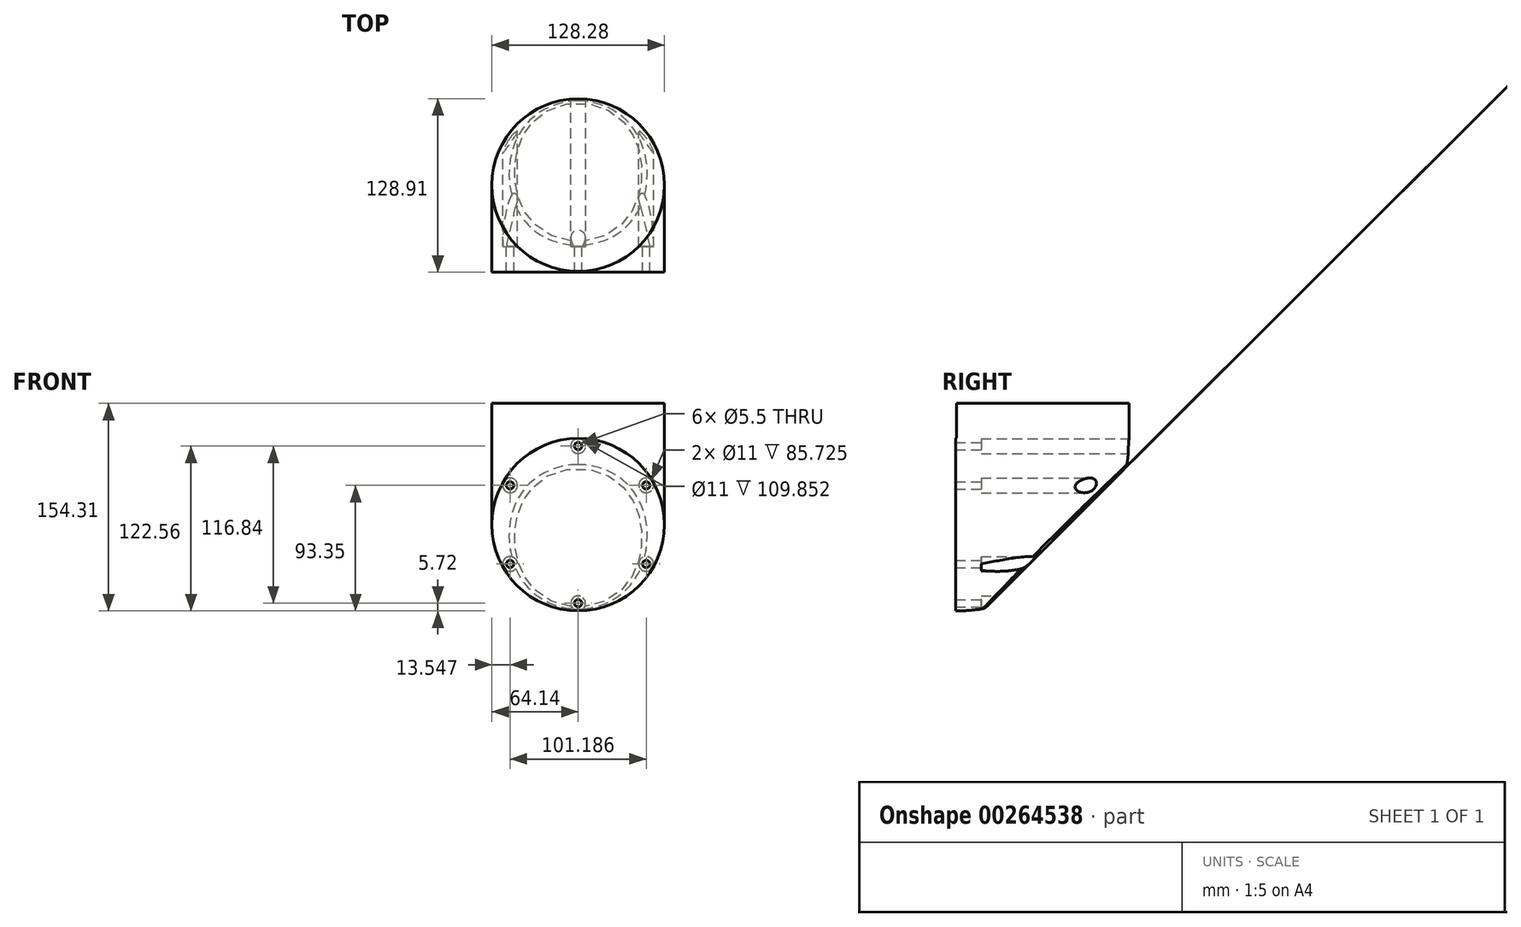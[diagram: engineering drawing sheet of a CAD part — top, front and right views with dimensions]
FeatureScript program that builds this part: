
annotation { "Feature Type Name" : "Feature", "Feature Type Description" : "" }
export const myFeature = defineFeature(function(context is Context, id is Id, definition is map)
    precondition{}
    {
        {
            var Q0;
            Q0=qCreatedBy(makeId("Front.planeOp"),FACE);
            var sketch = newSketch(context, id + "F0", { "sketchPlane" : qUnion([Q0])});
            skCircle(sketch, "E0", {"center": v(0, 0) * mm, "radius": 64.13 * mm});
            skSolve(sketch);
        }
        {
            var Q0;
            Q0=qCreatedBy(makeId("Right.planeOp"),FACE);
            var sketch = newSketch(context, id + "F1", { "sketchPlane" : qUnion([Q0])});
            skArc(sketch, "E1", {"start": v(0, 0) * mm, "mid": v(45.8, 18.97) * mm, "end": v(64.77, 64.77) * mm});
            skLineSegment(sketch, "E2", {"start": v(64.77, 64.77) * mm, "end": v(0, 64.77) * mm, "construction": true});
            skSolve(sketch);
        }
        {
            var Q0;
            Q0 = qSketchRegion(id + "F0", true);
            var Q1;
            Q1 = qConstructionFilter(qBodyType(qCreatedBy(id + "F1" ,EDGE), BodyType.WIRE), ConstructionObject.NO);
            sweep(context, id + "F2", {"profiles" : qUnion([Q0]), "path" : qUnion([Q1])});
        }
        {
            var Q0;
            Q0=qCreatedBy(makeId("Top.planeOp"),FACE);
            cPlane(context, id + "F3", {"entities" : qUnion([Q0]), "cplaneType" : CPlaneType.OFFSET, "offset" : 64.77 * mm, "width" : 152.4 * mm, "height" : 152.4 * mm});
        }
        {
            var Q0;
            Q0=qCreatedBy(id+"F3.planeOp",FACE);
            var sketch = newSketch(context, id + "F4", { "sketchPlane" : qUnion([Q0])});
            skPoint(sketch, "E3", {"position": v(0, 64.77) * mm});
            skLineSegment(sketch, "E4", {"start": v(0, 64.77) * mm, "end": v(0, 0) * mm, "construction": true});
            skCircle(sketch, "E5", {"center": v(0, 64.77) * mm, "radius": 50.8 * mm});
            skSolve(sketch);
        }
        {
            var Q0;
            Q0=makeQuery(id+"F2.opSweep","CAP_FACE",FACE,{"disambiguationData":[OSD([sQuery(id+"F0.wireOp",EDGE,"E0"),sQuery(id+"F1.wireOp",VERTEX,"E1.start")])],"isStart":true});
            var sketch = newSketch(context, id + "F5", { "sketchPlane" : qUnion([Q0])});
            skCircle(sketch, "E6", {"center": v(0, 0) * mm, "radius": 58.42 * mm, "construction": true});
            skPoint(sketch, "E7", {"position": v(0, 58.42) * mm});
            skPoint(sketch, "E8.1.0", {"position": v(-50.6, 29.21) * mm});
            skPoint(sketch, "E8.2.0", {"position": v(-50.6, -29.2) * mm});
            skPoint(sketch, "E8.3.0", {"position": v(0, -58.42) * mm});
            skPoint(sketch, "E8.4.0", {"position": v(50.6, -29.21) * mm});
            skPoint(sketch, "E8.5.0", {"position": v(50.6, 29.21) * mm});
            skSolve(sketch);
        }
        {
            var Q0;
            Q0=sQuery(id+"F5.wireOp",VERTEX,"E7");
            var Q1;
            Q1=sQuery(id+"F5.wireOp",VERTEX,"E8.1.0");
            var Q2;
            Q2=sQuery(id+"F5.wireOp",VERTEX,"E8.2.0");
            var Q3;
            Q3=sQuery(id+"F5.wireOp",VERTEX,"E8.3.0");
            var Q4;
            Q4=sQuery(id+"F5.wireOp",VERTEX,"E8.4.0");
            var Q5;
            Q5=sQuery(id+"F5.wireOp",VERTEX,"E8.5.0");
            var Q6;
            Q6=makeQuery(id+"F2.opSweep","SWEPT_BODY",BODY,{"disambiguationData":[OSD([sQuery(id+"F0.wireOp",EDGE,"E0"),sQuery(id+"F1.wireOp",EDGE,"E1")])]});
            hole(context, id + "F6", {"style" : HoleStyle.SIMPLE, "endStyle" : HoleEndStyle.THROUGH, "standardTappedOrClearance" : lookupTablePath({ "standard" : "ISO", "fit" : "Normal", "size" : "M5", "type" : "Clearance" }), "standardBlindInLast" : lookupTablePath({ "fit" : "Standard", "standard" : "ISO", "size" : "M5", "type" : "Clearance" }), "holeDiameter" : 5.5 * mm, "isTappedThrough" : true, "tappedDepth" : 12.7 * mm, "tapClearance" : 3, "locations" : qUnion([Q0, Q1, Q2, Q3, Q4, Q5]), "scope" : qUnion([Q6]), "startStyle" : HoleStartStyle.PART});
        }
        {
            var Q0;
            Q0=qCreatedBy(makeId("Front.planeOp"),FACE);
            cPlane(context, id + "F7", {"entities" : qUnion([Q0]), "cplaneType" : CPlaneType.OFFSET, "offset" : 19.05 * mm, "oppositeDirection" : true, "width" : 152.4 * mm, "height" : 152.4 * mm});
        }
        {
            var Q0;
            Q0=qCreatedBy(id+"F7.planeOp",FACE);
            var sketch = newSketch(context, id + "F8", { "sketchPlane" : qUnion([Q0])});
            skCircle(sketch, "E9", {"center": v(0, 0) * mm, "radius": 58.42 * mm, "construction": true});
            skPoint(sketch, "E10", {"position": v(0, 58.42) * mm});
            skPoint(sketch, "E11.1.0", {"position": v(-50.6, 29.21) * mm});
            skPoint(sketch, "E11.2.0", {"position": v(-50.6, -29.2) * mm});
            skPoint(sketch, "E11.3.0", {"position": v(0, -58.42) * mm});
            skPoint(sketch, "E11.4.0", {"position": v(50.6, -29.21) * mm});
            skPoint(sketch, "E11.5.0", {"position": v(50.6, 29.21) * mm});
            skSolve(sketch);
        }
        {
            var Q0;
            Q0=sQuery(id+"F8.wireOp",VERTEX,"E11.5.0");
            var Q1;
            Q1=sQuery(id+"F8.wireOp",VERTEX,"E11.4.0");
            var Q2;
            Q2=sQuery(id+"F8.wireOp",VERTEX,"E11.3.0");
            var Q3;
            Q3=sQuery(id+"F8.wireOp",VERTEX,"E11.2.0");
            var Q4;
            Q4=sQuery(id+"F8.wireOp",VERTEX,"E11.1.0");
            var Q5;
            Q5=sQuery(id+"F8.wireOp",VERTEX,"E10");
            var Q6;
            Q6=makeQuery(id+"F2.opSweep","SWEPT_BODY",BODY,{"disambiguationData":[OSD([sQuery(id+"F0.wireOp",EDGE,"E0"),sQuery(id+"F1.wireOp",EDGE,"E1")])]});
            hole(context, id + "F9", {"style" : HoleStyle.SIMPLE, "endStyle" : HoleEndStyle.THROUGH, "standardTappedOrClearance" : lookupTablePath({ "standard" : "ISO", "fit" : "Normal", "size" : "M10", "type" : "Clearance" }), "standardBlindInLast" : lookupTablePath({ "fit" : "Standard", "standard" : "ISO", "size" : "M10", "type" : "Clearance" }), "holeDiameter" : 11 * mm, "isTappedThrough" : true, "tappedDepth" : 12.7 * mm, "tapClearance" : 3, "locations" : qUnion([Q0, Q1, Q2, Q3, Q4, Q5]), "scope" : qUnion([Q6]), "startStyle" : HoleStartStyle.PART});
        }
        {
            var Q0;
            Q0=makeQuery(id+"F2.opSweep","CAP_FACE",FACE,{"disambiguationData":[OSD([sQuery(id+"F0.wireOp",EDGE,"E0"),sQuery(id+"F1.wireOp",VERTEX,"E1.end")])],"isStart":false});
            var sketch = newSketch(context, id + "F10", { "sketchPlane" : qUnion([Q0])});
            skCircle(sketch, "E12", {"center": v(0, 64.77) * mm, "radius": 64.13 * mm});
            skSolve(sketch);
        }
        {
            var Q0;
            Q0 = qSketchRegion(id + "F10", true);
            extrude(context, id + "F11", {"entities" : qUnion([Q0]), "operationType" : NewBodyOperationType.ADD, "depth" : 25.4 * mm, "offsetDistance" : 25.4 * mm});
        }
        {
            var Q0;
            Q0=qCreatedBy(makeId("Front.planeOp"),FACE);
            var Q1;
            Q1=qCreatedBy(makeId("Top.planeOp"),FACE);
            cPlane(context, id + "F12", {"entities" : qUnion([Q0, Q1]), "cplaneType" : CPlaneType.MID_PLANE, "offset" : 25.4 * mm, "flipAlignment" : true, "width" : 152.4 * mm, "height" : 152.4 * mm});
        }
        {
            var Q0;
            Q0=qCreatedBy(id+"F12.planeOp",FACE);
            var sketch = newSketch(context, id + "F13", { "sketchPlane" : qUnion([Q0])});
            skLineSegment(sketch, "E13.bottom", {"start": v(114.3, -54.54) * mm, "end": v(-114.3, -54.54) * mm});
            skLineSegment(sketch, "E13.top", {"start": v(114.3, 174.06) * mm, "end": v(-114.3, 174.06) * mm});
            skLineSegment(sketch, "E13.left", {"start": v(114.3, -54.54) * mm, "end": v(114.3, 174.06) * mm});
            skLineSegment(sketch, "E13.right", {"start": v(-114.3, -54.54) * mm, "end": v(-114.3, 174.06) * mm});
            skPoint(sketch, "E13.middle", {"position": v(0, 59.76) * mm});
            skSolve(sketch);
        }
        {
            var Q0;
            Q0=makeQuery(id+"F13.imprint","IMPRINT",FACE,{"disambiguationData":[TD([[makeQuery(id+"F13.imprint","IMPRINT",EDGE,{"derivedFrom":sQuery(id+"F13.wireOp",EDGE,"E13.bottom")}),-1.0]])]});
            extrude(context, id + "F14", {"entities" : qUnion([Q0]), "operationType" : NewBodyOperationType.REMOVE, "endBound" : BoundingType.THROUGH_ALL, "oppositeDirection" : true, "depth" : 25.4 * mm, "offsetDistance" : 25.4 * mm, "hasSecondDirection" : true, "secondDirectionOppositeDirection" : true, "secondDirectionDepth" : 59.44 * mm});
        }
        {
            var Q0;
            Q0=makeQuery(id+"F14.boolean.opBoolean","INTERSECT",EDGE,{"disambiguationData":[OD(1.0)],"derivedFrom":[makeQuery(id+"F2.opSweep","SWEPT_FACE",FACE,{"disambiguationData":[OSD([sQuery(id+"F0.wireOp",EDGE,"E0"),sQuery(id+"F1.wireOp",EDGE,"E1")])]}),makeQuery(id+"F14.opExtrude","CAP_FACE",FACE,{"disambiguationData":[OSD([sQuery(id+"F13.wireOp",EDGE,"E13.bottom"),sQuery(id+"F13.wireOp",EDGE,"E13.top"),sQuery(id+"F13.wireOp",EDGE,"E13.left"),sQuery(id+"F13.wireOp",EDGE,"E13.right")])],"isStart":true})]});
            var Q1;
            Q1=makeQuery(id+"F14.boolean.opBoolean","INTERSECT",EDGE,{"disambiguationData":[OD(2.0)],"derivedFrom":[makeQuery(id+"F2.opSweep","SWEPT_FACE",FACE,{"disambiguationData":[OSD([sQuery(id+"F0.wireOp",EDGE,"E0"),sQuery(id+"F1.wireOp",EDGE,"E1")])]}),makeQuery(id+"F14.opExtrude","CAP_FACE",FACE,{"disambiguationData":[OSD([sQuery(id+"F13.wireOp",EDGE,"E13.bottom"),sQuery(id+"F13.wireOp",EDGE,"E13.top"),sQuery(id+"F13.wireOp",EDGE,"E13.left"),sQuery(id+"F13.wireOp",EDGE,"E13.right")])],"isStart":true})]});
            var Q2;
            Q2=makeQuery(id+"F14.boolean.opBoolean","INTERSECT",EDGE,{"disambiguationData":[OD(0.0)],"derivedFrom":[makeQuery(id+"F2.opSweep","SWEPT_FACE",FACE,{"disambiguationData":[OSD([sQuery(id+"F0.wireOp",EDGE,"E0"),sQuery(id+"F1.wireOp",EDGE,"E1")])]}),makeQuery(id+"F14.opExtrude","CAP_FACE",FACE,{"disambiguationData":[OSD([sQuery(id+"F13.wireOp",EDGE,"E13.bottom"),sQuery(id+"F13.wireOp",EDGE,"E13.top"),sQuery(id+"F13.wireOp",EDGE,"E13.left"),sQuery(id+"F13.wireOp",EDGE,"E13.right")])],"isStart":true})]});
            fillet(context, id + "F15", {"entities" : qUnion([Q0, Q1, Q2]), "radius" : 5.08 * mm, "tangentPropagation" : true, "allowEdgeOverflow" : false});
        }
    });
